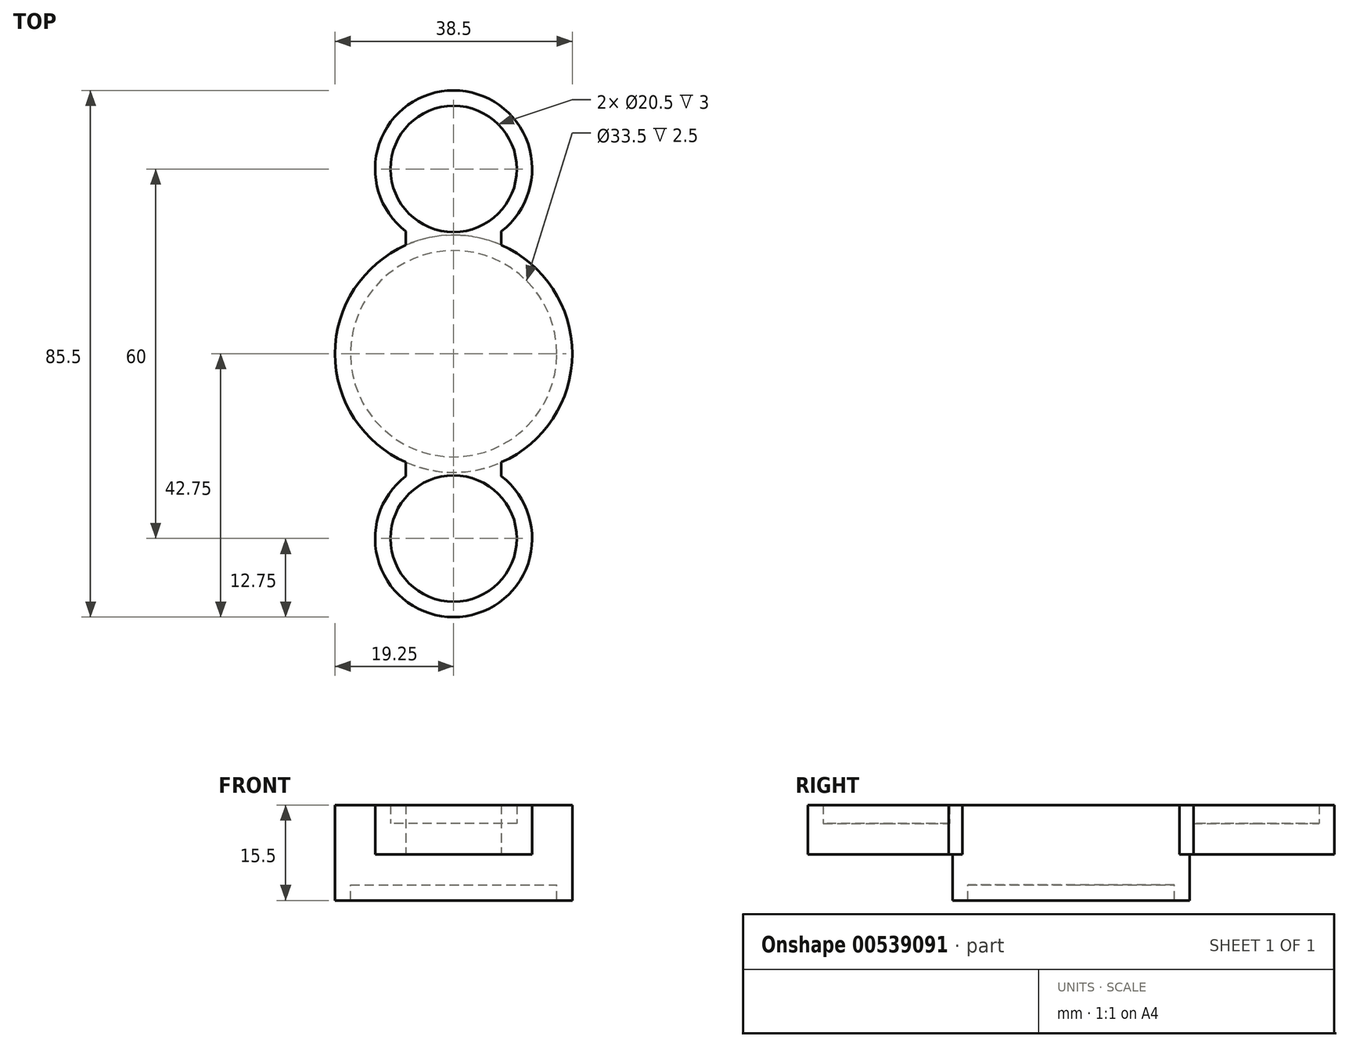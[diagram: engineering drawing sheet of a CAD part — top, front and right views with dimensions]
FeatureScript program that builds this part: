
annotation { "Feature Type Name" : "Feature", "Feature Type Description" : "" }
export const myFeature = defineFeature(function(context is Context, id is Id, definition is map)
    precondition{}
    {
        {
            var Q0;
            Q0=qCreatedBy(makeId("Top.planeOp"),FACE);
            var sketch = newSketch(context, id + "F0", { "sketchPlane" : qUnion([Q0])});
            skLineSegment(sketch, "E0", {"start": v(0, 0) * mm, "end": v(0, -2.5) * mm});
            skLineSegment(sketch, "E1", {"start": v(0, -2.5) * mm, "end": v(-2.5, -2.5) * mm});
            skLineSegment(sketch, "E2.bottom", {"start": v(-2.5, -2.5) * mm, "end": v(13, -2.5) * mm});
            skLineSegment(sketch, "E2.top", {"start": v(-2.5, 63) * mm, "end": v(13, 63) * mm});
            skLineSegment(sketch, "E2.left", {"start": v(-2.5, -2.5) * mm, "end": v(-2.5, 63) * mm});
            skLineSegment(sketch, "E2.right", {"start": v(13, -2.5) * mm, "end": v(13, 63) * mm});
            skLineSegment(sketch, "E3", {"start": v(5.25, 30.25) * mm, "end": v(5.25, 60.25) * mm});
            skLineSegment(sketch, "E4", {"start": v(5.25, 60.25) * mm, "end": v(5.25, 30.25) * mm});
            skLineSegment(sketch, "E5", {"start": v(5.25, 30.25) * mm, "end": v(5.25, 0.25) * mm});
            skCircle(sketch, "E6", {"center": v(5.25, 0.25) * mm, "radius": 10.25 * mm});
            skCircle(sketch, "E7", {"center": v(5.25, 60.25) * mm, "radius": 10.25 * mm});
            skCircle(sketch, "E8", {"center": v(5.25, 60.25) * mm, "radius": 12.75 * mm});
            skCircle(sketch, "E9", {"center": v(5.25, 0.25) * mm, "radius": 12.75 * mm});
            skSolve(sketch);
        }
        {
            var Q0;
            {var subQ1=sQuery(id+"F0.wireOp",EDGE,"E2.right");var subQ7=sQuery(id+"F0.wireOp",EDGE,"E9");var subQ9=makeQuery(id+"F0.imprint","INTERSECT",VERTEX,{"derivedFrom":[subQ1,subQ7]});Q0=makeQuery(id+"F0.imprint","IMPRINT",FACE,{"disambiguationData":[TD([[makeQuery(id+"F0.imprint","IMPRINT",EDGE,{"disambiguationData":[TD([[subQ9,-1.0]])],"derivedFrom":subQ1}),1.0]])]});}
            var Q1;
            {var subQ0=sQuery(id+"F0.wireOp",EDGE,"E8");var subQ1=sQuery(id+"F0.wireOp",EDGE,"E2.left");var subQ2=makeQuery(id+"F0.imprint","INTERSECT",VERTEX,{"derivedFrom":[subQ1,subQ0]});Q1=makeQuery(id+"F0.imprint","IMPRINT",FACE,{"disambiguationData":[TD([[makeQuery(id+"F0.imprint","IMPRINT",EDGE,{"disambiguationData":[TD([[subQ2,-1.0]])],"derivedFrom":subQ1}),1.0]])]});}
            var Q2;
            {var subQ0=sQuery(id+"F0.wireOp",EDGE,"E9");var subQ1=sQuery(id+"F0.wireOp",EDGE,"E2.left");var subQ2=makeQuery(id+"F0.imprint","INTERSECT",VERTEX,{"derivedFrom":[subQ1,subQ0]});Q2=makeQuery(id+"F0.imprint","IMPRINT",FACE,{"disambiguationData":[TD([[makeQuery(id+"F0.imprint","IMPRINT",EDGE,{"disambiguationData":[TD([[subQ2,1.0]])],"derivedFrom":subQ1}),1.0]])]});}
            var Q3;
            {var subQ1=sQuery(id+"F0.wireOp",EDGE,"E2.left");var subQ7=sQuery(id+"F0.wireOp",EDGE,"E9");var subQ9=makeQuery(id+"F0.imprint","INTERSECT",VERTEX,{"derivedFrom":[subQ1,subQ7]});Q3=makeQuery(id+"F0.imprint","IMPRINT",FACE,{"disambiguationData":[TD([[makeQuery(id+"F0.imprint","IMPRINT",EDGE,{"disambiguationData":[TD([[subQ9,-1.0]])],"derivedFrom":subQ1}),-1.0]])]});}
            var Q4;
            {var subQ0=sQuery(id+"F0.wireOp",EDGE,"E8");var subQ1=sQuery(id+"F0.wireOp",EDGE,"E2.left");var subQ2=makeQuery(id+"F0.imprint","INTERSECT",VERTEX,{"derivedFrom":[subQ1,subQ0]});Q4=makeQuery(id+"F0.imprint","IMPRINT",FACE,{"disambiguationData":[TD([[makeQuery(id+"F0.imprint","IMPRINT",EDGE,{"disambiguationData":[TD([[subQ2,-1.0]])],"derivedFrom":subQ1}),-1.0]])]});}
            var Q5;
            {var subQ0=sQuery(id+"F0.wireOp",EDGE,"E9");var subQ1=sQuery(id+"F0.wireOp",EDGE,"E2.left");var subQ2=makeQuery(id+"F0.imprint","INTERSECT",VERTEX,{"derivedFrom":[subQ1,subQ0]});Q5=makeQuery(id+"F0.imprint","IMPRINT",FACE,{"disambiguationData":[TD([[makeQuery(id+"F0.imprint","IMPRINT",EDGE,{"disambiguationData":[TD([[subQ2,1.0]])],"derivedFrom":subQ1}),-1.0]])]});}
            var Q6;
            {var subQ0=sQuery(id+"F0.wireOp",EDGE,"E8");var subQ1=sQuery(id+"F0.wireOp",EDGE,"E2.right");var subQ2=makeQuery(id+"F0.imprint","INTERSECT",VERTEX,{"derivedFrom":[subQ1,subQ0]});Q6=makeQuery(id+"F0.imprint","IMPRINT",FACE,{"disambiguationData":[TD([[makeQuery(id+"F0.imprint","IMPRINT",EDGE,{"disambiguationData":[TD([[subQ2,-1.0]])],"derivedFrom":subQ1}),1.0]])]});}
            var Q7;
            {var subQ0=sQuery(id+"F0.wireOp",EDGE,"E9");var subQ1=sQuery(id+"F0.wireOp",EDGE,"E2.right");var subQ2=makeQuery(id+"F0.imprint","INTERSECT",VERTEX,{"derivedFrom":[subQ1,subQ0]});Q7=makeQuery(id+"F0.imprint","IMPRINT",FACE,{"disambiguationData":[TD([[makeQuery(id+"F0.imprint","IMPRINT",EDGE,{"disambiguationData":[TD([[subQ2,1.0]])],"derivedFrom":subQ1}),1.0]])]});}
            extrude(context, id + "F1", {"entities" : qUnion([Q0, Q1, Q2, Q3, Q4, Q5, Q6, Q7]), "depth" : 5 * mm, "offsetDistance" : 25 * mm});
        }
        {
            var Q0;
            Q0=makeQuery(id+"F1.opExtrude","CAP_FACE",FACE,{"disambiguationData":[OSD([sQuery(id+"F0.wireOp",EDGE,"E2.left"),sQuery(id+"F0.wireOp",EDGE,"E2.right"),sQuery(id+"F0.wireOp",EDGE,"E6"),sQuery(id+"F0.wireOp",EDGE,"E7"),sQuery(id+"F0.wireOp",EDGE,"E8"),sQuery(id+"F0.wireOp",EDGE,"E9")])],"isStart":true});
            var sketch = newSketch(context, id + "F2", { "sketchPlane" : qUnion([Q0])});
            skArc(sketch, "E10", {"start": v(13, -10.37) * mm, "mid": v(5.25, 12.5) * mm, "end": v(-2.5, -10.37) * mm});
            skCircle(sketch, "E11", {"center": v(5.25, -60.25) * mm, "radius": 12.75 * mm});
            skLineSegment(sketch, "E12", {"start": v(5.25, -0.25) * mm, "end": v(5.25, -60.25) * mm});
            skLineSegment(sketch, "E13.left", {"start": v(13, -50.13) * mm, "end": v(13, -10.37) * mm});
            skLineSegment(sketch, "E13.right", {"start": v(-2.5, -50.13) * mm, "end": v(-2.5, -10.37) * mm});
            skPoint(sketch, "E13.middle", {"position": v(5.25, -30.25) * mm});
            skPoint(sketch, "E14.orphan", {"position": v(-2.5, -0.25) * mm});
            skPoint(sketch, "E15.orphan", {"position": v(13, -0.25) * mm});
            skPoint(sketch, "E16.orphan", {"position": v(-2.5, -60.25) * mm});
            skPoint(sketch, "E13.bottom.start.orphan", {"position": v(13, -60.25) * mm});
            skSolve(sketch);
        }
        {
            var Q0;
            Q0 = qSketchRegion(id + "F2", true);
            extrude(context, id + "F3", {"entities" : qUnion([Q0]), "operationType" : NewBodyOperationType.ADD, "depth" : 5 * mm, "offsetDistance" : 25 * mm});
        }
        {
            var Q0;
            Q0=makeQuery(id+"F3.opExtrude","CAP_FACE",FACE,{"disambiguationData":[OSD([sQuery(id+"F2.wireOp",EDGE,"E10"),sQuery(id+"F2.wireOp",EDGE,"E11"),sQuery(id+"F2.wireOp",EDGE,"E13.left"),sQuery(id+"F2.wireOp",EDGE,"E13.right")])],"isStart":false});
            var sketch = newSketch(context, id + "F4", { "sketchPlane" : qUnion([Q0])});
            skLineSegment(sketch, "E17", {"start": v(-2.5, -30.25) * mm, "end": v(13, -30.25) * mm});
            skCircle(sketch, "E18", {"center": v(5.25, -30.25) * mm, "radius": 19.25 * mm});
            skSolve(sketch);
        }
        {
            var Q0;
            Q0 = qSketchRegion(id + "F4", true);
            extrude(context, id + "F5", {"entities" : qUnion([Q0]), "operationType" : NewBodyOperationType.ADD, "oppositeDirection" : true, "depth" : 10 * mm, "offsetDistance" : 25 * mm});
        }
        {
            var Q0;
            Q0=makeQuery(id+"F5.boolean.opBoolean","MERGE",FACE,{"derivedFrom":[makeQuery(id+"F3.opExtrude","CAP_FACE",FACE,{"disambiguationData":[OSD([sQuery(id+"F2.wireOp",EDGE,"E10"),sQuery(id+"F2.wireOp",EDGE,"E11"),sQuery(id+"F2.wireOp",EDGE,"E13.left"),sQuery(id+"F2.wireOp",EDGE,"E13.right")])],"isStart":false}),makeQuery(id+"F5.opExtrude","CAP_FACE",FACE,{"disambiguationData":[OSD([sQuery(id+"F4.wireOp",EDGE,"E18")])],"isStart":true})]});
            var sketch = newSketch(context, id + "F6", { "sketchPlane" : qUnion([Q0])});
            skCircle(sketch, "E19", {"center": v(5.25, -30.25) * mm, "radius": 19.25 * mm});
            skCircle(sketch, "E20", {"center": v(5.25, -30.25) * mm, "radius": 16.75 * mm});
            skSolve(sketch);
        }
        {
            var Q0;
            Q0=makeQuery(id+"F6.imprint","IMPRINT",FACE,{"disambiguationData":[TD([[makeQuery(id+"F6.imprint","IMPRINT",EDGE,{"derivedFrom":sQuery(id+"F6.wireOp",EDGE,"E20")}),-1.0]])]});
            extrude(context, id + "F7", {"entities" : qUnion([Q0]), "operationType" : NewBodyOperationType.ADD, "depth" : 2.5 * mm, "offsetDistance" : 25 * mm});
        }
        {
            var Q0;
            Q0=makeQuery(id+"F5.boolean.opBoolean","MERGE",FACE,{"derivedFrom":[makeQuery(id+"F1.opExtrude","CAP_FACE",FACE,{"disambiguationData":[OSD([sQuery(id+"F0.wireOp",EDGE,"E2.left"),sQuery(id+"F0.wireOp",EDGE,"E2.right"),sQuery(id+"F0.wireOp",EDGE,"E6"),sQuery(id+"F0.wireOp",EDGE,"E7"),sQuery(id+"F0.wireOp",EDGE,"E8"),sQuery(id+"F0.wireOp",EDGE,"E9")])],"isStart":false}),makeQuery(id+"F5.opExtrude","CAP_FACE",FACE,{"disambiguationData":[OSD([sQuery(id+"F4.wireOp",EDGE,"E18")])],"isStart":false})]});
            extrude(context, id + "F8", {"entities" : qUnion([Q0]), "operationType" : NewBodyOperationType.REMOVE, "oppositeDirection" : true, "depth" : 2 * mm, "offsetDistance" : 25 * mm});
        }
        {
            var Q0;
            Q0=makeQuery(id+"F7.boolean.opBoolean","SPLIT",FACE,{"disambiguationData":[TD([makeQuery(id+"F7.opExtrude","SWEPT_FACE",FACE,{"disambiguationData":[OSD([sQuery(id+"F6.wireOp",EDGE,"E20")])]})])],"derivedFrom":makeQuery(id+"F5.boolean.opBoolean","MERGE",FACE,{"derivedFrom":[makeQuery(id+"F3.opExtrude","CAP_FACE",FACE,{"disambiguationData":[OSD([sQuery(id+"F2.wireOp",EDGE,"E10"),sQuery(id+"F2.wireOp",EDGE,"E11"),sQuery(id+"F2.wireOp",EDGE,"E13.left"),sQuery(id+"F2.wireOp",EDGE,"E13.right")])],"isStart":false}),makeQuery(id+"F5.opExtrude","CAP_FACE",FACE,{"disambiguationData":[OSD([sQuery(id+"F4.wireOp",EDGE,"E18")])],"isStart":true})]})});
            var Q1;
            Q1=makeQuery(id+"F7.opExtrude","CAP_FACE",FACE,{"disambiguationData":[OSD([sQuery(id+"F6.wireOp",EDGE,"E19"),sQuery(id+"F6.wireOp",EDGE,"E20")])],"isStart":false});
            extrude(context, id + "F9", {"entities" : qUnion([Q0, Q1]), "operationType" : NewBodyOperationType.ADD, "depth" : 5 * mm, "offsetDistance" : 25 * mm});
        }
    });
